# Revit family: Mixer-Bath Shower-Caroma Contura with Diverter1
name_source: partatom
category: Plumbing Fixtures
revit_build: Autodesk Revit 2014 (Build: 20140709_2115(x64)
units: mm (PartAtom-declared; Revit-internal decimal feet)

## types (1)
- Standard
    Assembly Code = C1030210
    CW Connection = Yes
    CWFU = 3
    Connector Radius = 10 mm  [stored 0.0328084 ft]
    Cost = 0 $
    Default Elevation = 1000 mm  [stored 3.28084 ft]
    HW Connection = Yes
    HWFU = 3
    Height_ANZRS = 175 mm  [stored 0.574147 ft]
    Length_ANZRS = 80 mm  [stored 0.262467 ft]
    Manufacturer = GWA Bathrooms & Kitchens
    Material_ANZRS = Metal-Chrome-Caroma
    Model = 99586C
    ModifiedIssue_ANZRS = 20151016 $
    Type Comments = Caroma Contura Bath/Shower Mixer with Diverter
    URL = http://specify.caroma.com.au
    Vent Connection = No
    Waste Connection = No
    Width_ANZRS = 72 mm  [stored 0.23622 ft]

note: [stored X ft] marks values corroborated as IEEE doubles in the binary element streams (Revit-internal decimal feet)

## geometry (parser evidence)
native form markers: Blend x10, Sweep x1
no freeform markers — native parametric forms only
